# Revit family: Shower-Shower_Column_Kit-KOHLER-HydroRail-K-76474
name_source: partatom
category: Plumbing Fixtures
revit_build: Autodesk Revit 2015 (Build: 20140606_1530(x64)
units: mm (PartAtom-declared; Revit-internal decimal feet)

## types (2) — shared parameters
ADA Compliant = No
Assembly Code = D2010700
CW Connection = No
Cold Water Inlet = Cold Water Inlet
Date Modified = 04/08/2019
Default Elevation = 72"
Description = Arch shower column kit with Awaken rainhead and Shift Ellipse handshower, 2.0 gpm
Drain Included = No
Flow Rate = 2 GPM
HW Connection = Yes
Height = 18"
Hot Water Inlet = Tempered Water Inlet
Length = 17 15/16"
Manufacturer = KOHLER Co.
MasterFormat 1995 = 15410
MasterFormat 2004 = 22.41.23
Material = Premium Metal Construction
Panel Thickness = 0"
Product Documentation Link = https://www.us.kohler.com
Product Name = HydroRail
Product Page URL = http://www.us.kohler.com
URL = https://www.us.kohler.com
Vent Connection = No
Waste Connection = No
Waste Water Outlet = Waste Water Outlet
WaterSense Certified = No
Width = 3"

## per-type parameters (varying)
| type | Finish | Model | Type |
| BN-Vibrant Brushed Nickel | Kohler-Metal-BN-Vibrant_Brushed_Nickel | K-76474-BN | 2 |
| CP-Polished Chrome | Kohler-Metal-CP-Polished_Chrome | K-76474-CP | 1 |

## geometry (parser evidence)
native form markers: Sweep x6
no freeform markers — native parametric forms only
